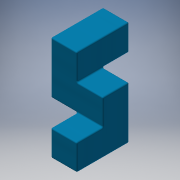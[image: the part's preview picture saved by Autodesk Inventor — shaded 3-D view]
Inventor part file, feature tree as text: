
AUTODESK INVENTOR PART (.ipt)
format: ipt  version: 2016 (Build 200138000, 138)  size: 183,808 bytes
history: native  units: in
note: dims shown in document units (in); Inventor stores cm internally (conversion verified against a paired STEP export)
features: plane x8, extrude x3, other x1, fillet x1, sketch x1
ambient origin geometry x8: Origin, YZ Plane, XZ Plane, XY Plane, X Axis, Y Axis, Z Axis, Center Point
bodies: Solid1 (feature_tree)
feature tree (14):
  other  "Cube Master.ipt"
  extrude  "Extrusion1"  Depth=0.3937in
  extrude  "Extrusion2"  Depth=0.0193in TaperAngle=0.0deg
  extrude  "Extrusion3"  Depth=0.0193in TaperAngle=0.0deg
  fillet  "Fillet1"  Radius=1.0in
  sketch  "Sketch1"  dims[d0=0.3937in d1=0.3937in d2=1.0in d3=0.0in d4=1.0in d5=0.0in d6=1.0in d7=0.0in d9=0.0193in d10=0.0193in]
  plane  "Work Plane1"
  plane  "Work Plane2"
  plane  "Work Plane3"
  plane  "Work Plane4"
  plane  "Work Plane5"
  plane  "Work Plane6"
  plane  "Work Plane7"
  plane  "Work Plane8"
